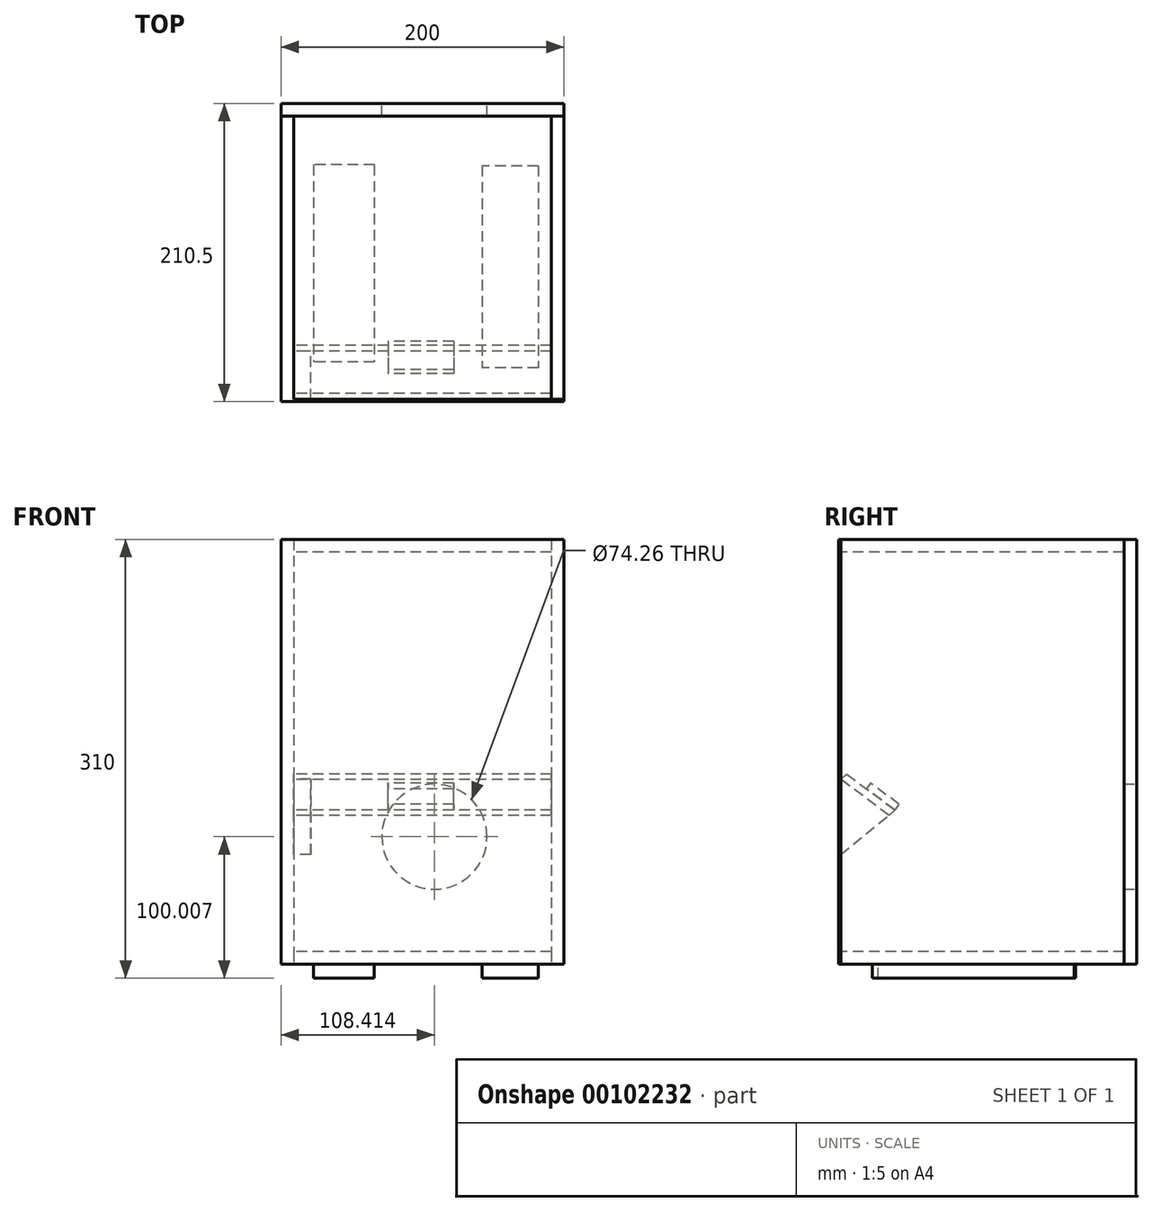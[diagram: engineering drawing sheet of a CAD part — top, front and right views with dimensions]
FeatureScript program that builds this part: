
annotation { "Feature Type Name" : "Feature", "Feature Type Description" : "" }
export const myFeature = defineFeature(function(context is Context, id is Id, definition is map)
    precondition{}
    {
        {
            var Q0;
            Q0=qCreatedBy(makeId("Front.planeOp"),FACE);
            var sketch = newSketch(context, id + "F0", { "sketchPlane" : qUnion([Q0])});
            skLineSegment(sketch, "E0.bottom", {"start": v(0, 0) * mm, "end": v(200, 0) * mm});
            skLineSegment(sketch, "E0.top", {"start": v(0, 300) * mm, "end": v(200, 300) * mm});
            skLineSegment(sketch, "E0.left", {"start": v(0, 0) * mm, "end": v(0, 300) * mm});
            skLineSegment(sketch, "E0.right", {"start": v(200, 0) * mm, "end": v(200, 300) * mm});
            skSolve(sketch);
        }
        {
            var Q0;
            Q0 = qSketchRegion(id + "F0", true);
            extrude(context, id + "F1", {"entities" : qUnion([Q0]), "depth" : 1.5 * mm});
        }
        {
            var Q0;
            Q0=makeQuery(id+"F1.opExtrude","CAP_FACE",FACE,{"disambiguationData":[OSD([sQuery(id+"F0.wireOp",EDGE,"E0.bottom"),sQuery(id+"F0.wireOp",EDGE,"E0.top"),sQuery(id+"F0.wireOp",EDGE,"E0.left"),sQuery(id+"F0.wireOp",EDGE,"E0.right")])],"isStart":true});
            var sketch = newSketch(context, id + "F2", { "sketchPlane" : qUnion([Q0])});
            skLineSegment(sketch, "E1.bottom", {"start": v(0, 300) * mm, "end": v(-9, 300) * mm});
            skLineSegment(sketch, "E1.top", {"start": v(0, 0) * mm, "end": v(-9, 0) * mm});
            skLineSegment(sketch, "E1.left", {"start": v(0, 300) * mm, "end": v(0, 0) * mm});
            skLineSegment(sketch, "E1.right", {"start": v(-9, 300) * mm, "end": v(-9, 0) * mm});
            skSolve(sketch);
        }
        {
            var Q0;
            Q0 = qSketchRegion(id + "F2", true);
            extrude(context, id + "F3", {"entities" : qUnion([Q0]), "operationType" : NewBodyOperationType.ADD, "depth" : 200 * mm});
        }
        {
            var Q0;
            Q0=makeQuery(id+"F3.opExtrude","SWEPT_FACE",FACE,{"disambiguationData":[OSD([sQuery(id+"F2.wireOp",EDGE,"E1.right")])]});
            var sketch = newSketch(context, id + "F4", { "sketchPlane" : qUnion([Q0])});
            skLineSegment(sketch, "E2", {"start": v(0, 130.62) * mm, "end": v(0, 77.52) * mm});
            skLineSegment(sketch, "E3", {"start": v(0, 77.52) * mm, "end": v(34.06, 105.11) * mm});
            skLineSegment(sketch, "E4", {"start": v(34.06, 105.11) * mm, "end": v(0, 130.62) * mm});
            skSolve(sketch);
        }
        {
            var Q0;
            Q0 = qSketchRegion(id + "F4", true);
            extrude(context, id + "F5", {"entities" : qUnion([Q0]), "depth" : 12 * mm});
        }
        {
            var Q0;
            Q0=makeQuery(id+"F3.opExtrude","SWEPT_FACE",FACE,{"disambiguationData":[OSD([sQuery(id+"F2.wireOp",EDGE,"E1.right")])]});
            var sketch = newSketch(context, id + "F6", { "sketchPlane" : qUnion([Q0])});
            skLineSegment(sketch, "E5", {"start": v(34.06, 105.11) * mm, "end": v(0, 130.56) * mm});
            skLineSegment(sketch, "E6", {"start": v(0, 130.56) * mm, "end": v(4.1, 134.28) * mm});
            skLineSegment(sketch, "E7", {"start": v(4.1, 134.28) * mm, "end": v(38.17, 108.83) * mm});
            skLineSegment(sketch, "E8", {"start": v(38.17, 108.83) * mm, "end": v(34.06, 105.11) * mm});
            skSolve(sketch);
        }
        {
            var Q0;
            Q0=makeQuery(id+"F6.imprint","IMPRINT",FACE,{"disambiguationData":[TD([[makeQuery(id+"F6.imprint","IMPRINT",EDGE,{"derivedFrom":sQuery(id+"F6.wireOp",EDGE,"E5")}),-1.0]])]});
            extrude(context, id + "F7", {"entities" : qUnion([Q0]), "depth" : 182 * mm});
        }
        {
            var Q0;
            Q0=makeQuery(id+"F7.opExtrude","SWEPT_FACE",FACE,{"disambiguationData":[OSD([sQuery(id+"F6.wireOp",EDGE,"E7")])]});
            var sketch = newSketch(context, id + "F8", { "sketchPlane" : qUnion([Q0])});
            skLineSegment(sketch, "E9.bottom", {"start": v(121.99, -34.56) * mm, "end": v(75.6, -34.56) * mm});
            skLineSegment(sketch, "E9.top", {"start": v(121.99, -59.68) * mm, "end": v(75.6, -59.68) * mm});
            skLineSegment(sketch, "E9.left", {"start": v(121.99, -34.56) * mm, "end": v(121.99, -59.68) * mm});
            skLineSegment(sketch, "E9.right", {"start": v(75.6, -34.56) * mm, "end": v(75.6, -59.68) * mm});
            skSolve(sketch);
        }
        {
            var Q0;
            Q0=makeQuery(id+"F8.imprint","IMPRINT",FACE,{"disambiguationData":[TD([[makeQuery(id+"F8.imprint","IMPRINT",EDGE,{"derivedFrom":sQuery(id+"F8.wireOp",EDGE,"E9.bottom")}),1.0]])]});
            extrude(context, id + "F9", {"entities" : qUnion([Q0]), "depth" : 5 * mm});
        }
        {
            var Q0;
            Q0=makeQuery(id+"F3.opExtrude","SWEPT_FACE",FACE,{"disambiguationData":[OSD([sQuery(id+"F2.wireOp",EDGE,"E1.right")])]});
            var sketch = newSketch(context, id + "F10", { "sketchPlane" : qUnion([Q0])});
            skLineSegment(sketch, "E10.bottom", {"start": v(200, 300) * mm, "end": v(0, 300) * mm});
            skLineSegment(sketch, "E10.top", {"start": v(200, 291) * mm, "end": v(0, 291) * mm});
            skLineSegment(sketch, "E10.left", {"start": v(200, 300) * mm, "end": v(200, 291) * mm});
            skLineSegment(sketch, "E10.right", {"start": v(0, 300) * mm, "end": v(0, 291) * mm});
            skSolve(sketch);
        }
        {
            var Q0;
            Q0 = qSketchRegion(id + "F10", true);
            extrude(context, id + "F11", {"entities" : qUnion([Q0]), "depth" : 182 * mm});
        }
        {
            var Q0;
            Q0=makeQuery(id+"F3.opExtrude","SWEPT_FACE",FACE,{"disambiguationData":[OSD([sQuery(id+"F2.wireOp",EDGE,"E1.right")])]});
            var sketch = newSketch(context, id + "F12", { "sketchPlane" : qUnion([Q0])});
            skLineSegment(sketch, "E11.bottom", {"start": v(200, 0) * mm, "end": v(0, 0) * mm});
            skLineSegment(sketch, "E11.top", {"start": v(200, 9) * mm, "end": v(0, 9) * mm});
            skLineSegment(sketch, "E11.left", {"start": v(200, 0) * mm, "end": v(200, 9) * mm});
            skLineSegment(sketch, "E11.right", {"start": v(0, 0) * mm, "end": v(0, 9) * mm});
            skSolve(sketch);
        }
        {
            var Q0;
            Q0=makeQuery(id+"F12.imprint","IMPRINT",FACE,{"disambiguationData":[TD([[makeQuery(id+"F12.imprint","IMPRINT",EDGE,{"derivedFrom":sQuery(id+"F12.wireOp",EDGE,"E11.bottom")}),-1.0]])]});
            extrude(context, id + "F13", {"entities" : qUnion([Q0]), "depth" : 182 * mm});
        }
        {
            var Q0;
            Q0=makeQuery(id+"F11.opExtrude","CAP_FACE",FACE,{"disambiguationData":[OSD([sQuery(id+"F10.wireOp",EDGE,"E10.bottom"),sQuery(id+"F10.wireOp",EDGE,"E10.top"),sQuery(id+"F10.wireOp",EDGE,"E10.left"),sQuery(id+"F10.wireOp",EDGE,"E10.right")])],"isStart":false});
            var sketch = newSketch(context, id + "F14", { "sketchPlane" : qUnion([Q0])});
            skLineSegment(sketch, "E12.bottom", {"start": v(200, 300) * mm, "end": v(0, 300) * mm});
            skLineSegment(sketch, "E12.top", {"start": v(200, 0) * mm, "end": v(0, 0) * mm});
            skLineSegment(sketch, "E12.left", {"start": v(200, 300) * mm, "end": v(200, 0) * mm});
            skLineSegment(sketch, "E12.right", {"start": v(0, 300) * mm, "end": v(0, 0) * mm});
            skSolve(sketch);
        }
        {
            var Q0;
            Q0 = qSketchRegion(id + "F14", true);
            extrude(context, id + "F15", {"entities" : qUnion([Q0]), "depth" : 9 * mm});
        }
        {
            var Q0;
            Q0=makeQuery(id+"F15.opExtrude","SWEPT_FACE",FACE,{"disambiguationData":[OSD([sQuery(id+"F14.wireOp",EDGE,"E12.left")])]});
            var sketch = newSketch(context, id + "F16", { "sketchPlane" : qUnion([Q0])});
            skLineSegment(sketch, "E13.bottom", {"start": v(-200, 300) * mm, "end": v(0, 300) * mm});
            skLineSegment(sketch, "E13.top", {"start": v(-200, 0) * mm, "end": v(0, 0) * mm});
            skLineSegment(sketch, "E13.left", {"start": v(-200, 300) * mm, "end": v(-200, 0) * mm});
            skLineSegment(sketch, "E13.right", {"start": v(0, 300) * mm, "end": v(0, 0) * mm});
            skSolve(sketch);
        }
        {
            var Q0;
            Q0 = qSketchRegion(id + "F16", true);
            extrude(context, id + "F17", {"entities" : qUnion([Q0]), "depth" : 9 * mm});
        }
        {
            var Q0;
            Q0=makeQuery(id+"F17.opExtrude","CAP_FACE",FACE,{"disambiguationData":[OSD([sQuery(id+"F16.wireOp",EDGE,"E13.bottom"),sQuery(id+"F16.wireOp",EDGE,"E13.top"),sQuery(id+"F16.wireOp",EDGE,"E13.left"),sQuery(id+"F16.wireOp",EDGE,"E13.right")])],"isStart":false});
            var sketch = newSketch(context, id + "F18", { "sketchPlane" : qUnion([Q0])});
            skCircle(sketch, "E14", {"center": v(-108.41, 90) * mm, "radius": 37.13 * mm});
            skSolve(sketch);
        }
        {
            var Q0;
            Q0=makeQuery(id+"F18.imprint","IMPRINT",FACE,{"disambiguationData":[TD([[makeQuery(id+"F18.imprint","IMPRINT",EDGE,{"derivedFrom":sQuery(id+"F18.wireOp",EDGE,"E14")}),1.0]])]});
            extrude(context, id + "F19", {"entities" : qUnion([Q0]), "operationType" : NewBodyOperationType.REMOVE, "oppositeDirection" : true, "depth" : 9 * mm});
        }
        {
            var Q0;
            Q0=makeQuery(id+"F13.opExtrude","SWEPT_FACE",FACE,{"disambiguationData":[OSD([sQuery(id+"F12.wireOp",EDGE,"E11.bottom")])]});
            var sketch = newSketch(context, id + "F20", { "sketchPlane" : qUnion([Q0])});
            skLineSegment(sketch, "E15.bottom", {"start": v(181.79, -164.95) * mm, "end": v(142.03, -164.95) * mm});
            skLineSegment(sketch, "E15.top", {"start": v(181.79, -22.39) * mm, "end": v(142.03, -22.39) * mm});
            skLineSegment(sketch, "E15.left", {"start": v(181.79, -164.95) * mm, "end": v(181.79, -22.39) * mm});
            skLineSegment(sketch, "E15.right", {"start": v(142.03, -164.95) * mm, "end": v(142.03, -22.39) * mm});
            skSolve(sketch);
        }
        {
            var Q0;
            Q0=makeQuery(id+"F20.imprint","IMPRINT",FACE,{"disambiguationData":[TD([[makeQuery(id+"F20.imprint","IMPRINT",EDGE,{"derivedFrom":sQuery(id+"F20.wireOp",EDGE,"E15.bottom")}),-1.0]])]});
            extrude(context, id + "F21", {"entities" : qUnion([Q0]), "depth" : 10 * mm});
        }
        {
            var Q0;
            Q0=makeQuery(id+"F13.opExtrude","SWEPT_FACE",FACE,{"disambiguationData":[OSD([sQuery(id+"F12.wireOp",EDGE,"E11.bottom")])]});
            var sketch = newSketch(context, id + "F22", { "sketchPlane" : qUnion([Q0])});
            skLineSegment(sketch, "E16.bottom", {"start": v(66.02, -165.7) * mm, "end": v(22.86, -165.7) * mm});
            skLineSegment(sketch, "E16.top", {"start": v(66.02, -26.53) * mm, "end": v(22.86, -26.53) * mm});
            skLineSegment(sketch, "E16.left", {"start": v(66.02, -165.7) * mm, "end": v(66.02, -26.53) * mm});
            skLineSegment(sketch, "E16.right", {"start": v(22.86, -165.7) * mm, "end": v(22.86, -26.53) * mm});
            skSolve(sketch);
        }
        {
            var Q0;
            Q0=makeQuery(id+"F22.imprint","IMPRINT",FACE,{"disambiguationData":[TD([[makeQuery(id+"F22.imprint","IMPRINT",EDGE,{"derivedFrom":sQuery(id+"F22.wireOp",EDGE,"E16.bottom")}),-1.0]])]});
            extrude(context, id + "F23", {"entities" : qUnion([Q0]), "depth" : 10 * mm});
        }
    });
